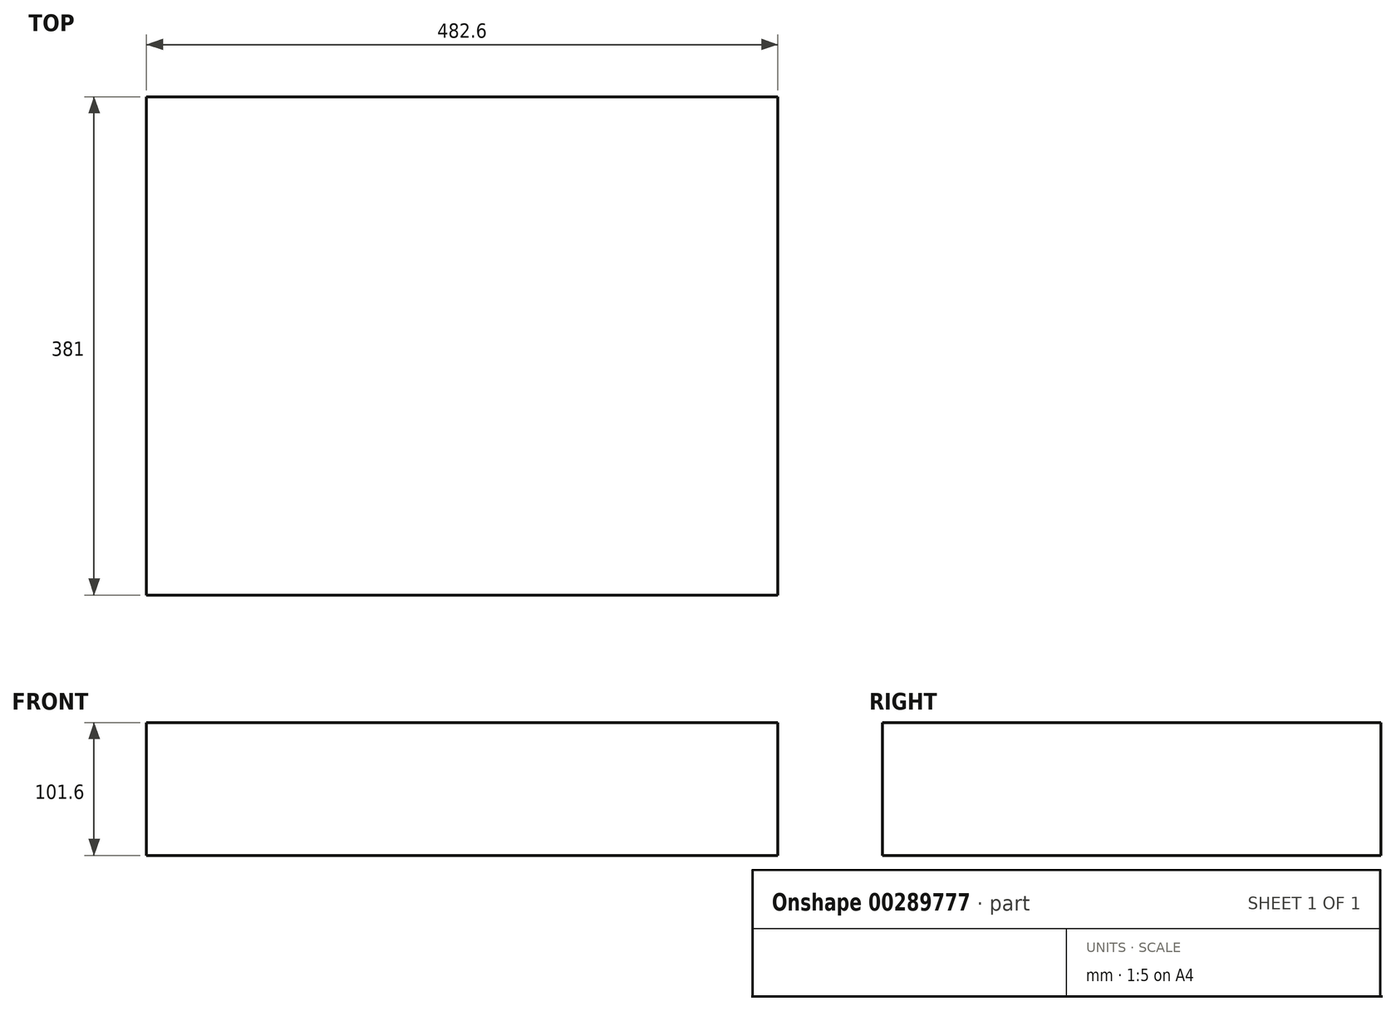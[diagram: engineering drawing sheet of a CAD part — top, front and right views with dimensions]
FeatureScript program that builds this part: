
annotation { "Feature Type Name" : "Feature", "Feature Type Description" : "" }
export const myFeature = defineFeature(function(context is Context, id is Id, definition is map)
    precondition{}
    {
        {
            var Q0;
            Q0=qCreatedBy(makeId("Top.planeOp"),FACE);
            var sketch = newSketch(context, id + "F0", { "sketchPlane" : qUnion([Q0])});
            skLineSegment(sketch, "E0.bottom", {"start": v(0, 0) * mm, "end": v(482.6, 0) * mm});
            skLineSegment(sketch, "E0.top", {"start": v(0, 381) * mm, "end": v(482.6, 381) * mm});
            skLineSegment(sketch, "E0.left", {"start": v(0, 0) * mm, "end": v(0, 381) * mm});
            skLineSegment(sketch, "E0.right", {"start": v(482.6, 0) * mm, "end": v(482.6, 381) * mm});
            skSolve(sketch);
        }
        {
            var Q0;
            Q0=makeQuery(id+"F0.imprint","IMPRINT",FACE,{"disambiguationData":[TD([[makeQuery(id+"F0.imprint","IMPRINT",EDGE,{"derivedFrom":sQuery(id+"F0.wireOp",EDGE,"E0.bottom")}),1.0]])]});
            extrude(context, id + "F1", {"entities" : qUnion([Q0]), "depth" : 101.6 * mm});
        }
    });
